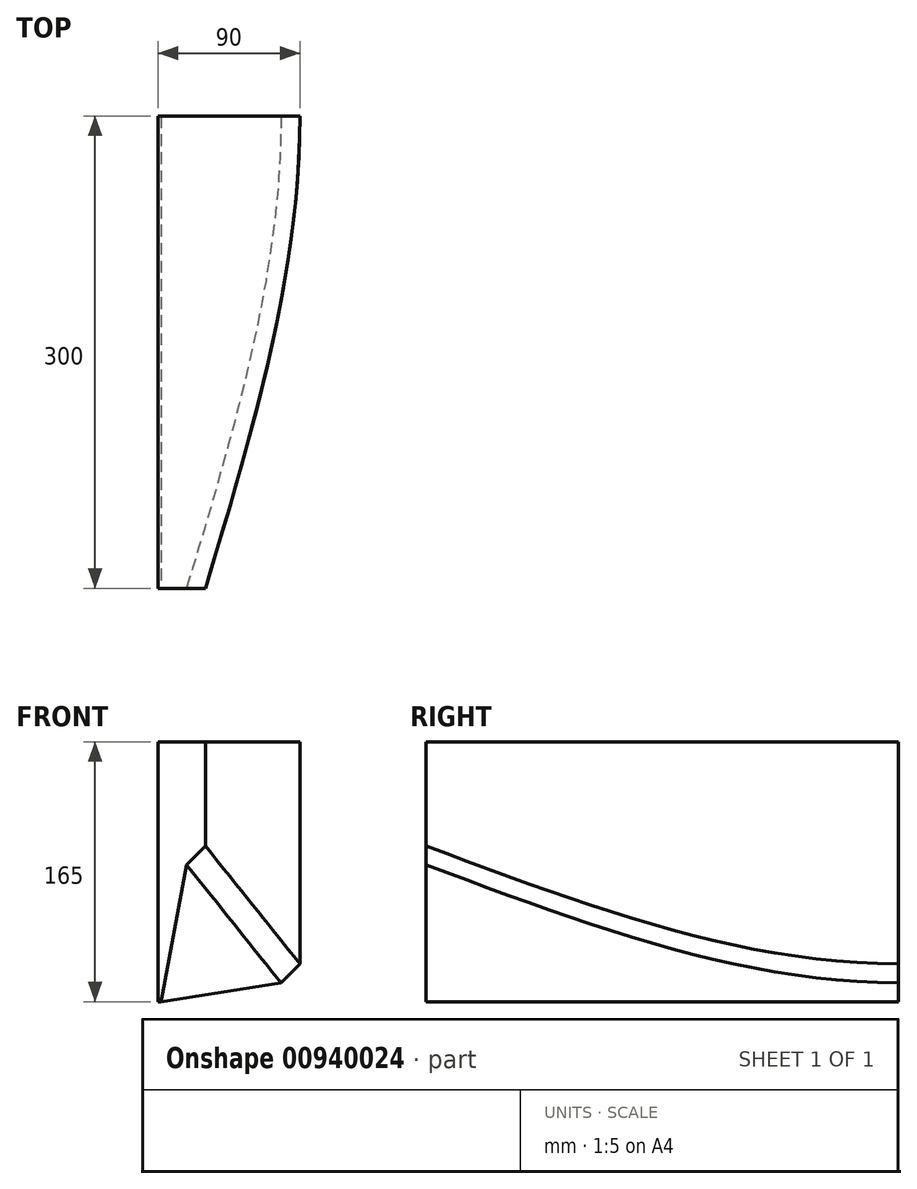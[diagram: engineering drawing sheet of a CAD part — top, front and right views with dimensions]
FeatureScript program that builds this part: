
annotation { "Feature Type Name" : "Feature", "Feature Type Description" : "" }
export const myFeature = defineFeature(function(context is Context, id is Id, definition is map)
    precondition{}
    {
        {
            var Q0;
            Q0=qCreatedBy(makeId("Front.planeOp"),FACE);
            var sketch = newSketch(context, id + "F0", { "sketchPlane" : qUnion([Q0])});
            skLineSegment(sketch, "E0", {"start": v(0, 0) * mm, "end": v(0, 90) * mm});
            skLineSegment(sketch, "E1", {"start": v(0, 90) * mm, "end": v(90, 90) * mm});
            skLineSegment(sketch, "E2", {"start": v(90, 90) * mm, "end": v(90, -51) * mm});
            skLineSegment(sketch, "E3", {"start": v(90, -51) * mm, "end": v(78, -63) * mm});
            skLineSegment(sketch, "E4", {"start": v(78, -63) * mm, "end": v(2, -75) * mm});
            skLineSegment(sketch, "E5", {"start": v(2, -75) * mm, "end": v(0, -75) * mm});
            skLineSegment(sketch, "E6", {"start": v(0, -75) * mm, "end": v(0, 0) * mm});
            skSolve(sketch);
        }
        {
            var Q0;
            Q0=qCreatedBy(makeId("Front.planeOp"),FACE);
            cPlane(context, id + "F1", {"entities" : qUnion([Q0]), "cplaneType" : CPlaneType.OFFSET, "offset" : 300 * mm, "width" : 150 * mm, "height" : 150 * mm});
        }
        {
            var Q0;
            Q0=qCreatedBy(id+"F1.planeOp",FACE);
            var sketch = newSketch(context, id + "F2", { "sketchPlane" : qUnion([Q0])});
            skLineSegment(sketch, "E7", {"start": v(0, 0) * mm, "end": v(0, 90) * mm});
            skLineSegment(sketch, "E8", {"start": v(0, 90) * mm, "end": v(30, 90) * mm});
            skLineSegment(sketch, "E9", {"start": v(30, 90) * mm, "end": v(30, 24) * mm});
            skLineSegment(sketch, "E10", {"start": v(30, 24) * mm, "end": v(18, 12) * mm});
            skLineSegment(sketch, "E11", {"start": v(18, 12) * mm, "end": v(2, -75) * mm});
            skLineSegment(sketch, "E12", {"start": v(2, -75) * mm, "end": v(0, -75) * mm});
            skLineSegment(sketch, "E13", {"start": v(0, -75) * mm, "end": v(0, 0) * mm});
            skSolve(sketch);
        }
        {
            var Q0;
            Q0=makeQuery(id+"F0.imprint","IMPRINT",FACE,{"disambiguationData":[TD([[makeQuery(id+"F0.imprint","IMPRINT",EDGE,{"derivedFrom":sQuery(id+"F0.wireOp",EDGE,"E0")}),-1.0]])]});
            var Q1;
            Q1=makeQuery(id+"F2.imprint","IMPRINT",FACE,{"disambiguationData":[TD([[makeQuery(id+"F2.imprint","IMPRINT",EDGE,{"derivedFrom":sQuery(id+"F2.wireOp",EDGE,"E7")}),-1.0]])]});
            loft(context, id + "F3", {"startCondition" : LoftEndDerivativeType.NORMAL_TO_PROFILE, "startMagnitude" : 1, "sheetProfilesArray" : [{ "sheetProfileEntities" : qUnion([Q0]) }, { "sheetProfileEntities" : qUnion([Q1]) }]});
        }
    });
